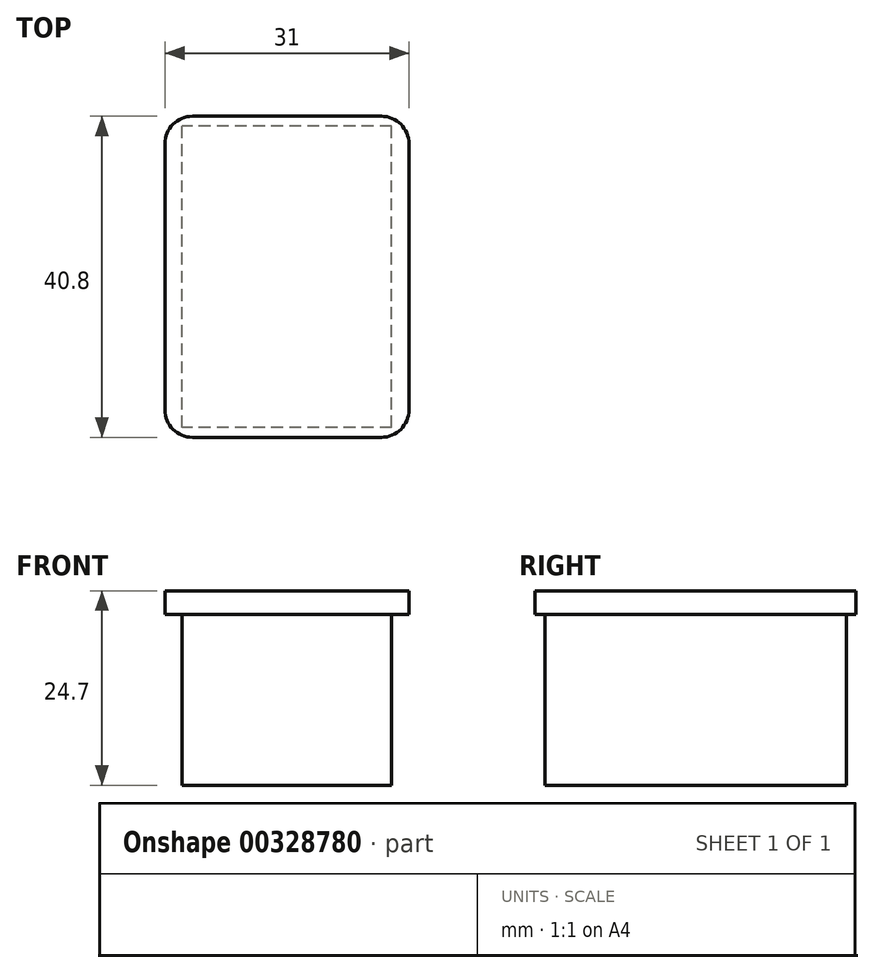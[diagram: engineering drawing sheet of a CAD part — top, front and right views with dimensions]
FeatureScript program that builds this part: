
annotation { "Feature Type Name" : "Feature", "Feature Type Description" : "" }
export const myFeature = defineFeature(function(context is Context, id is Id, definition is map)
    precondition{}
    {
        {
            var Q0;
            Q0=qCreatedBy(makeId("Top.planeOp"),FACE);
            var sketch = newSketch(context, id + "F0", { "sketchPlane" : qUnion([Q0])});
            skLineSegment(sketch, "E0.bottom", {"start": v(13.3, -19.15) * mm, "end": v(-13.3, -19.15) * mm});
            skLineSegment(sketch, "E0.top", {"start": v(13.3, 19.15) * mm, "end": v(-13.3, 19.15) * mm});
            skLineSegment(sketch, "E0.left", {"start": v(13.3, -19.15) * mm, "end": v(13.3, 19.15) * mm});
            skLineSegment(sketch, "E0.right", {"start": v(-13.3, -19.15) * mm, "end": v(-13.3, 19.15) * mm});
            skPoint(sketch, "E0.middle", {"position": v(0, 0) * mm});
            skSolve(sketch);
        }
        {
            var Q0;
            Q0=qSketchRegion(id+"F0",true);
            extrude(context, id + "F1", {"entities" : qUnion([Q0]), "depth" : 21.7 * mm});
        }
        {
            var Q0;
            Q0=makeQuery(id+"F1.opExtrude","CAP_FACE",FACE,{"disambiguationData":[OSD([sQuery(id+"F0.wireOp",EDGE,"E0.bottom"),sQuery(id+"F0.wireOp",EDGE,"E0.top"),sQuery(id+"F0.wireOp",EDGE,"E0.left"),sQuery(id+"F0.wireOp",EDGE,"E0.right")])],"isStart":false});
            var sketch = newSketch(context, id + "F2", { "sketchPlane" : qUnion([Q0])});
            skLineSegment(sketch, "E1.bottom", {"start": v(-12, 20.4) * mm, "end": v(12, 20.4) * mm});
            skLineSegment(sketch, "E1.top", {"start": v(-12, -20.4) * mm, "end": v(12, -20.4) * mm});
            skLineSegment(sketch, "E1.left", {"start": v(-15.5, 16.9) * mm, "end": v(-15.5, -16.9) * mm});
            skLineSegment(sketch, "E1.right", {"start": v(15.5, 16.9) * mm, "end": v(15.5, -16.9) * mm});
            skPoint(sketch, "E1.middle", {"position": v(0, 0) * mm});
            skPoint(sketch, "E2.visualSharp", {"position": v(-15.5, 20.4) * mm});
            skArc(sketch, "E2.filletArc", {"start": v(-12, 20.4) * mm, "mid": v(-14.47, 19.37) * mm, "end": v(-15.5, 16.9) * mm});
            skPoint(sketch, "E3.visualSharp", {"position": v(15.5, 20.4) * mm});
            skArc(sketch, "E3.filletArc", {"start": v(15.5, 16.9) * mm, "mid": v(14.47, 19.37) * mm, "end": v(12, 20.4) * mm});
            skPoint(sketch, "E4.visualSharp", {"position": v(15.5, -20.4) * mm});
            skArc(sketch, "E4.filletArc", {"start": v(12, -20.4) * mm, "mid": v(14.47, -19.37) * mm, "end": v(15.5, -16.9) * mm});
            skPoint(sketch, "E5.visualSharp", {"position": v(-15.5, -20.4) * mm});
            skArc(sketch, "E5.filletArc", {"start": v(-15.5, -16.9) * mm, "mid": v(-14.47, -19.37) * mm, "end": v(-12, -20.4) * mm});
            skSolve(sketch);
        }
        {
            var Q0;
            Q0=qSketchRegion(id+"F2",true);
            extrude(context, id + "F3", {"entities" : qUnion([Q0]), "operationType" : NewBodyOperationType.ADD, "depth" : 3 * mm});
        }
    });
